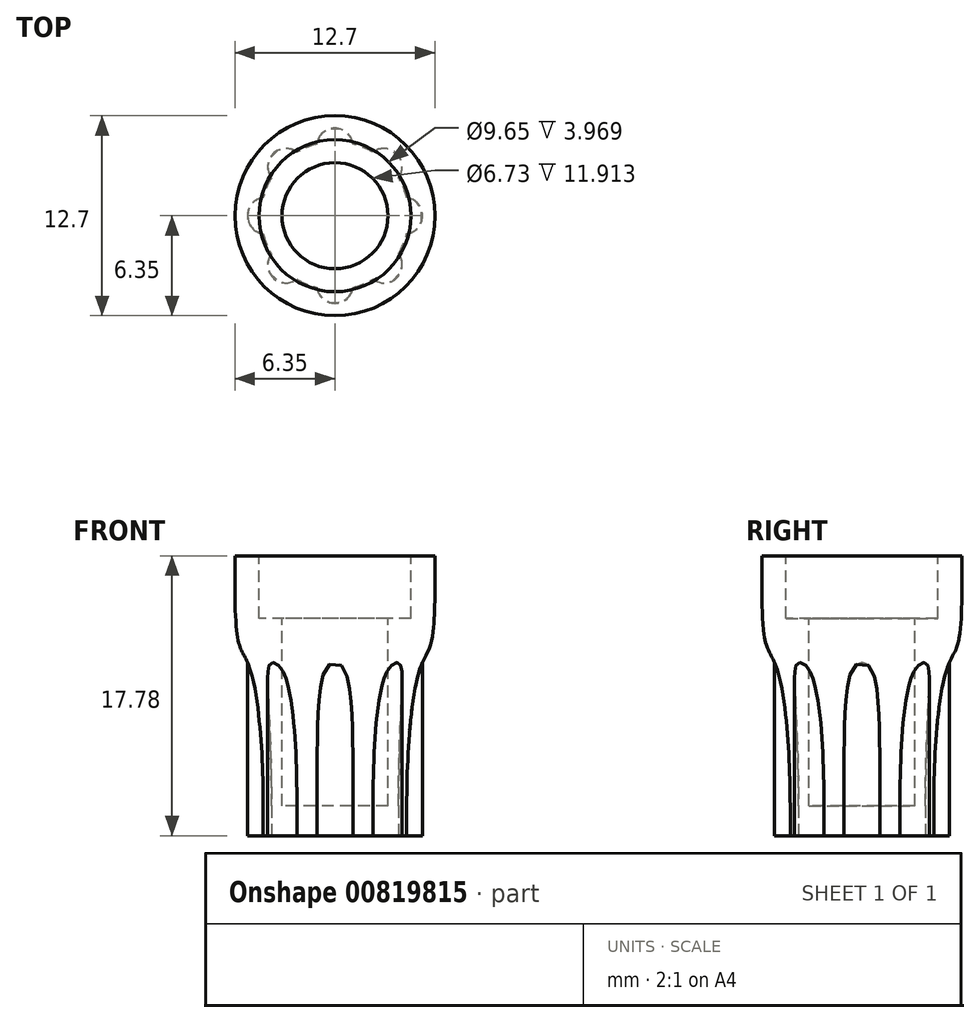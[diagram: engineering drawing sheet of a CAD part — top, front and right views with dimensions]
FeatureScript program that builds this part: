
annotation { "Feature Type Name" : "Feature", "Feature Type Description" : "" }
export const myFeature = defineFeature(function(context is Context, id is Id, definition is map)
    precondition{}
    {
        {
            var Q0;
            Q0=qCreatedBy(makeId("Top.planeOp"),FACE);
            var sketch = newSketch(context, id + "F0", { "sketchPlane" : qUnion([Q0])});
            skCircle(sketch, "E0", {"center": v(0, 0) * mm, "radius": 6.35 * mm});
            skCircle(sketch, "E1", {"center": v(0, 0) * mm, "radius": 4.83 * mm});
            skSolve(sketch);
        }
        {
            var Q0;
            Q0 = qSketchRegion(id + "F0", true);
            var Q1;
            Q1=makeQuery(id+"F0.imprint","IMPRINT",FACE,{"disambiguationData":[TD([[makeQuery(id+"F0.imprint","IMPRINT",EDGE,{"derivedFrom":sQuery(id+"F0.wireOp",EDGE,"E1")}),1.0]])]});
            extrude(context, id + "F1", {"entities" : qUnion([Q0, Q1]), "oppositeDirection" : true, "depth" : 17.78 * mm, "offsetDistance" : 25.4 * mm});
        }
        {
            var Q0;
            Q0=makeQuery(id+"F0.imprint","IMPRINT",FACE,{"disambiguationData":[TD([[makeQuery(id+"F0.imprint","IMPRINT",EDGE,{"derivedFrom":sQuery(id+"F0.wireOp",EDGE,"E1")}),1.0]])]});
            extrude(context, id + "F2", {"entities" : qUnion([Q0]), "operationType" : NewBodyOperationType.REMOVE, "oppositeDirection" : true, "depth" : 3.97 * mm, "offsetDistance" : 25.4 * mm});
        }
        {
            var Q0;
            Q0=makeQuery(id+"F2.boolean.opBoolean","COPY",FACE,{"derivedFrom":makeQuery(id+"F2.opExtrude","CAP_FACE",FACE,{"disambiguationData":[OSD([sQuery(id+"F0.wireOp",EDGE,"E1")])],"isStart":false})});
            var sketch = newSketch(context, id + "F3", { "sketchPlane" : qUnion([Q0])});
            skCircle(sketch, "E2", {"center": v(0, 0) * mm, "radius": 3.37 * mm});
            skSolve(sketch);
        }
        {
            var Q0;
            Q0=makeQuery(id+"F3.imprint","IMPRINT",FACE,{"disambiguationData":[TD([[makeQuery(id+"F3.imprint","IMPRINT",EDGE,{"derivedFrom":sQuery(id+"F3.wireOp",EDGE,"E2")}),1.0]])]});
            extrude(context, id + "F4", {"entities" : qUnion([Q0]), "operationType" : NewBodyOperationType.REMOVE, "oppositeDirection" : true, "depth" : 11.9 * mm, "offsetDistance" : 25.4 * mm});
        }
        {
            var Q0;
            Q0=qCreatedBy(makeId("Front.planeOp"),FACE);
            var sketch = newSketch(context, id + "F5", { "sketchPlane" : qUnion([Q0])});
            skLineSegment(sketch, "E3", {"start": v(0, 0) * mm, "end": v(0, -2.09) * mm, "construction": true});
            skLineSegment(sketch, "E4.0", {"start": v(-6.35, 0) * mm, "end": v(6.35, 0) * mm});
            skLineSegment(sketch, "E4.1", {"start": v(-4.83, 0) * mm, "end": v(4.83, 0) * mm});
            skLineSegment(sketch, "E4.2", {"start": v(-6.35, -17.78) * mm, "end": v(6.35, -17.78) * mm});
            skLineSegment(sketch, "E4.3", {"start": v(-4.83, -3.97) * mm, "end": v(4.83, -3.97) * mm, "construction": true});
            skLineSegment(sketch, "E4.4", {"start": v(-3.37, -3.97) * mm, "end": v(3.37, -3.97) * mm, "construction": true});
            skLineSegment(sketch, "E5.0", {"start": v(-3.37, -15.88) * mm, "end": v(3.37, -15.88) * mm, "construction": true});
            skLineSegment(sketch, "E6", {"start": v(-6.35, 0) * mm, "end": v(-6.35, -4.05) * mm});
            skPoint(sketch, "E7", {"position": v(-6.35, -3.97) * mm});
            skLineSegment(sketch, "E8", {"start": v(-3.37, -15.88) * mm, "end": v(-4.86, -15.88) * mm, "construction": true});
            skPoint(sketch, "E9", {"position": v(-4.86, -15.88) * mm});
            skLineSegment(sketch, "E10", {"start": v(-4.86, -15.88) * mm, "end": v(-6.35, -15.88) * mm, "construction": true});
            skLineSegment(sketch, "E11", {"start": v(-6.35, -4.05) * mm, "end": v(-6.35, -17.78) * mm});
            skPoint(sketch, "E12", {"position": v(-6.35, -2.02) * mm});
            skLineSegment(sketch, "E13", {"start": v(-6.35, -2.02) * mm, "end": v(-8.85, -2.02) * mm});
            skLineSegment(sketch, "E14", {"start": v(-8.85, -2.02) * mm, "end": v(-8.85, -19.2) * mm});
            skLineSegment(sketch, "E15", {"start": v(-8.85, -19.2) * mm, "end": v(-4.7, -19.2) * mm});
            skPoint(sketch, "E16", {"position": v(-4.7, -15.88) * mm});
            skPoint(sketch, "E17", {"position": v(0, -15.88) * mm});
            skFitSpline(sketch, "E18", {"points": [v(-6.35, -2.02) * mm, v(-5.56, -6.78) * mm, v(-4.7, -15.88) * mm], "startDerivative": vector(0, -29.62) * mm, "endDerivative": vector(0, -21.17) * mm});
            skLineSegment(sketch, "E19", {"start": v(-4.7, -15.88) * mm, "end": v(-4.7, -19.2) * mm});
            skSolve(sketch);
        }
        {
            var Q0;
            Q0 = qSketchRegion(id + "F5", true);
            var Q1;
            Q1=sQuery(id+"F5.wireOp",EDGE,"E3");
            revolve(context, id + "F6", {"operationType" : NewBodyOperationType.REMOVE, "surfaceOperationType" : NewSurfaceOperationType.NEW, "entities" : qUnion([Q0]), "axis" : qUnion([Q1]), "revolveType" : RevolveType.FULL, "oppositeDirection" : true});
        }
        {
            var Q0;
            Q0=makeQuery(id+"F1.opExtrude","CAP_FACE",FACE,{"disambiguationData":[OSD([sQuery(id+"F0.wireOp",EDGE,"E0")])],"isStart":false});
            var sketch = newSketch(context, id + "F7", { "sketchPlane" : qUnion([Q0])});
            skCircle(sketch, "E20.0", {"center": v(0, 0) * mm, "radius": 4.7 * mm});
            skArc(sketch, "E21", {"start": v(1.15, 4.56) * mm, "mid": v(0, 5.56) * mm, "end": v(-1.15, 4.56) * mm});
            skArc(sketch, "E22.1.0", {"start": v(-2.41, 4.03) * mm, "mid": v(-3.93, 3.93) * mm, "end": v(-4.03, 2.41) * mm});
            skArc(sketch, "E22.2.0", {"start": v(-4.56, 1.15) * mm, "mid": v(-5.56, 0) * mm, "end": v(-4.56, -1.15) * mm});
            skArc(sketch, "E22.3.0", {"start": v(-4.03, -2.41) * mm, "mid": v(-3.93, -3.93) * mm, "end": v(-2.41, -4.03) * mm});
            skArc(sketch, "E22.4.0", {"start": v(-1.15, -4.56) * mm, "mid": v(0, -5.56) * mm, "end": v(1.15, -4.56) * mm});
            skArc(sketch, "E22.5.0", {"start": v(2.41, -4.03) * mm, "mid": v(3.93, -3.93) * mm, "end": v(4.03, -2.41) * mm});
            skArc(sketch, "E22.6.0", {"start": v(4.56, -1.15) * mm, "mid": v(5.56, 0) * mm, "end": v(4.56, 1.15) * mm});
            skArc(sketch, "E22.7.0", {"start": v(4.03, 2.41) * mm, "mid": v(3.93, 3.93) * mm, "end": v(2.41, 4.03) * mm});
            skSolve(sketch);
        }
        {
            var Q0;
            {var subQ0=sQuery(id+"F7.wireOp",EDGE,"E22.5.0");Q0=makeQuery(id+"F7.imprint","IMPRINT",FACE,{"disambiguationData":[TD([[makeQuery(id+"F7.imprint","IMPRINT",EDGE,{"derivedFrom":subQ0}),1.0]])]});}
            var Q1;
            {var subQ0=sQuery(id+"F7.wireOp",EDGE,"E22.4.0");Q1=makeQuery(id+"F7.imprint","IMPRINT",FACE,{"disambiguationData":[TD([[makeQuery(id+"F7.imprint","IMPRINT",EDGE,{"derivedFrom":subQ0}),1.0]])]});}
            var Q2;
            {var subQ0=sQuery(id+"F7.wireOp",EDGE,"E22.3.0");Q2=makeQuery(id+"F7.imprint","IMPRINT",FACE,{"disambiguationData":[TD([[makeQuery(id+"F7.imprint","IMPRINT",EDGE,{"derivedFrom":subQ0}),1.0]])]});}
            var Q3;
            {var subQ0=sQuery(id+"F7.wireOp",EDGE,"E22.2.0");Q3=makeQuery(id+"F7.imprint","IMPRINT",FACE,{"disambiguationData":[TD([[makeQuery(id+"F7.imprint","IMPRINT",EDGE,{"derivedFrom":subQ0}),1.0]])]});}
            var Q4;
            {var subQ0=sQuery(id+"F7.wireOp",EDGE,"E22.1.0");Q4=makeQuery(id+"F7.imprint","IMPRINT",FACE,{"disambiguationData":[TD([[makeQuery(id+"F7.imprint","IMPRINT",EDGE,{"derivedFrom":subQ0}),1.0]])]});}
            var Q5;
            {var subQ0=sQuery(id+"F7.wireOp",EDGE,"E21");Q5=makeQuery(id+"F7.imprint","IMPRINT",FACE,{"disambiguationData":[TD([[makeQuery(id+"F7.imprint","IMPRINT",EDGE,{"derivedFrom":subQ0}),1.0]])]});}
            var Q6;
            {var subQ0=sQuery(id+"F7.wireOp",EDGE,"E22.7.0");Q6=makeQuery(id+"F7.imprint","IMPRINT",FACE,{"disambiguationData":[TD([[makeQuery(id+"F7.imprint","IMPRINT",EDGE,{"derivedFrom":subQ0}),1.0]])]});}
            var Q7;
            {var subQ0=sQuery(id+"F7.wireOp",EDGE,"E22.6.0");Q7=makeQuery(id+"F7.imprint","IMPRINT",FACE,{"disambiguationData":[TD([[makeQuery(id+"F7.imprint","IMPRINT",EDGE,{"derivedFrom":subQ0}),1.0]])]});}
            extrude(context, id + "F8", {"entities" : qUnion([Q0, Q1, Q2, Q3, Q4, Q5, Q6, Q7]), "operationType" : NewBodyOperationType.ADD, "oppositeDirection" : true, "depth" : 11.1 * mm, "offsetDistance" : 25.4 * mm});
        }
    });
